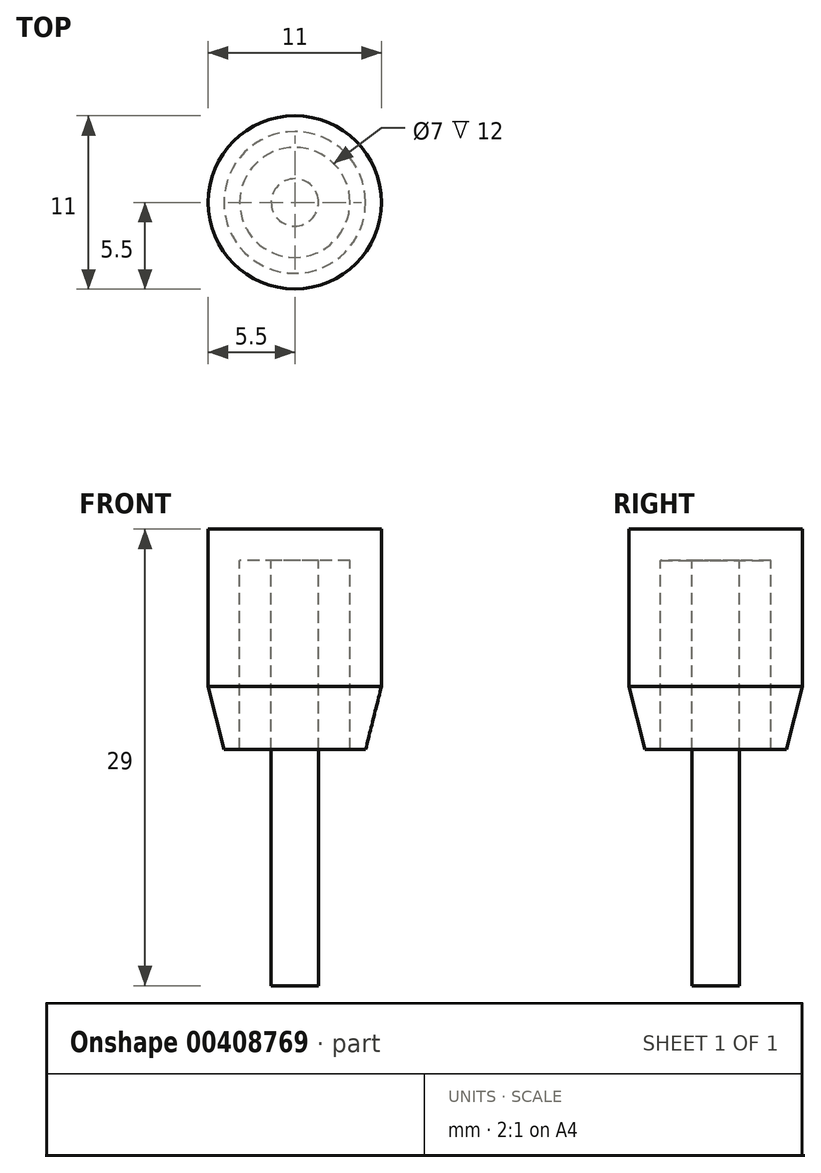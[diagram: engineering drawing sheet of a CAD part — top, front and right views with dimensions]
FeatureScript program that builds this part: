
annotation { "Feature Type Name" : "Feature", "Feature Type Description" : "" }
export const myFeature = defineFeature(function(context is Context, id is Id, definition is map)
    precondition{}
    {
        {
            var Q0;
            Q0=qCreatedBy(makeId("Top.planeOp"),FACE);
            var sketch = newSketch(context, id + "F0", { "sketchPlane" : qUnion([Q0])});
            skCircle(sketch, "E0", {"center": v(0, 0) * mm, "radius": 3.5 * mm});
            skCircle(sketch, "E1", {"center": v(0, 0) * mm, "radius": 5.5 * mm});
            skCircle(sketch, "E2", {"center": v(0, 0) * mm, "radius": 1.5 * mm});
            skSolve(sketch);
        }
        {
            var Q0;
            Q0=makeQuery(id+"F0.imprint","IMPRINT",FACE,{"disambiguationData":[TD([[makeQuery(id+"F0.imprint","IMPRINT",EDGE,{"derivedFrom":sQuery(id+"F0.wireOp",EDGE,"E0")}),-1.0]])]});
            var Q1;
            Q1=makeQuery(id+"F0.imprint","IMPRINT",FACE,{"disambiguationData":[TD([[makeQuery(id+"F0.imprint","IMPRINT",EDGE,{"derivedFrom":sQuery(id+"F0.wireOp",EDGE,"E2")}),1.0]])]});
            var Q2;
            Q2=makeQuery(id+"F0.imprint","IMPRINT",FACE,{"disambiguationData":[TD([[makeQuery(id+"F0.imprint","IMPRINT",EDGE,{"derivedFrom":sQuery(id+"F0.wireOp",EDGE,"E0")}),1.0]])]});
            var Q3;
            Q3=sQuery(id+"F0.wireOp",EDGE,"E1");
            extrude(context, id + "F1", {"entities" : qUnion([Q0, Q1, Q2]), "surfaceEntities" : qUnion([Q3]), "depth" : 2 * mm});
        }
        {
            var Q0;
            Q0=makeQuery(id+"F0.imprint","IMPRINT",FACE,{"disambiguationData":[TD([[makeQuery(id+"F0.imprint","IMPRINT",EDGE,{"derivedFrom":sQuery(id+"F0.wireOp",EDGE,"E2")}),1.0]])]});
            var Q1;
            Q1=sQuery(id+"F0.wireOp",EDGE,"E2");
            extrude(context, id + "F2", {"entities" : qUnion([Q0]), "operationType" : NewBodyOperationType.ADD, "surfaceEntities" : qUnion([Q1]), "oppositeDirection" : true, "depth" : 27 * mm});
        }
        {
            var Q0;
            Q0=makeQuery(id+"F0.imprint","IMPRINT",FACE,{"disambiguationData":[TD([[makeQuery(id+"F0.imprint","IMPRINT",EDGE,{"derivedFrom":sQuery(id+"F0.wireOp",EDGE,"E0")}),-1.0]])]});
            extrude(context, id + "F3", {"entities" : qUnion([Q0]), "operationType" : NewBodyOperationType.ADD, "oppositeDirection" : true, "depth" : 12 * mm});
        }
        {
            var Q0;
            Q0=makeQuery(id+"F3.opExtrude","CAP_EDGE",EDGE,{"disambiguationData":[OSD([sQuery(id+"F0.wireOp",EDGE,"E1")])],"isStart":false});
            chamfer(context, id + "F4", {"entities" : qUnion([Q0]), "chamferType" : ChamferType.TWO_OFFSETS, "width1" : 4 * mm, "oppositeDirection" : false, "width2" : 1 * mm, "tangentPropagation" : true});
        }
    });
